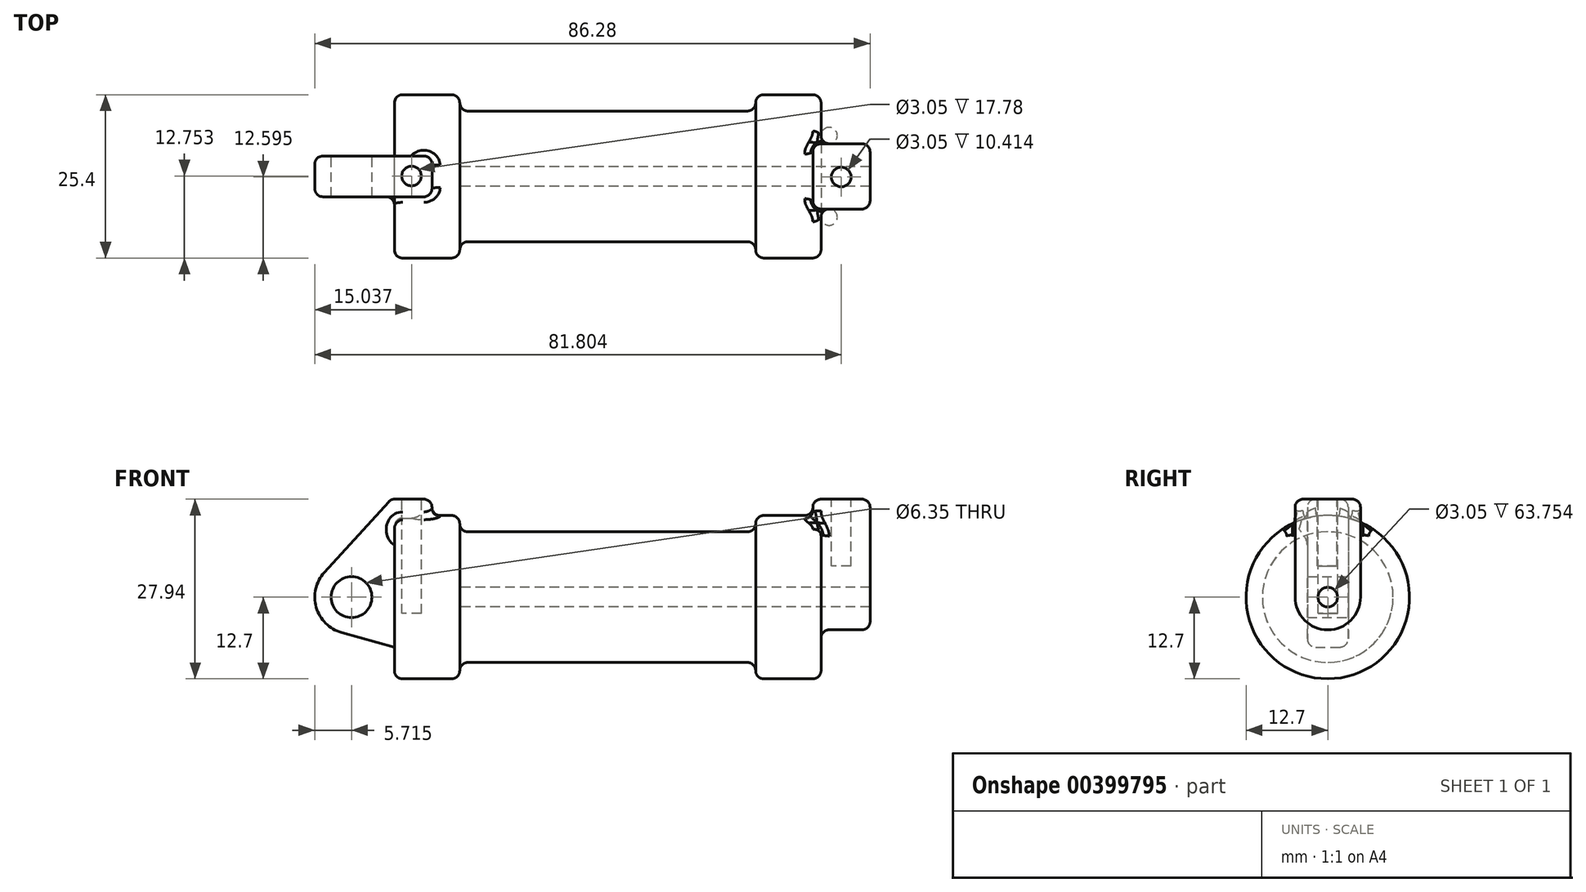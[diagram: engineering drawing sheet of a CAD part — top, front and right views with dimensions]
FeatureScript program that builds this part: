
annotation { "Feature Type Name" : "Feature", "Feature Type Description" : "" }
export const myFeature = defineFeature(function(context is Context, id is Id, definition is map)
    precondition{}
    {
        {
            var Q0;
            Q0=qCreatedBy(makeId("Front.planeOp"),FACE);
            var sketch = newSketch(context, id + "F0", { "sketchPlane" : qUnion([Q0])});
            skLineSegment(sketch, "E0", {"start": v(0, 0) * mm, "end": v(0, 12.7) * mm});
            skLineSegment(sketch, "E1", {"start": v(0, 12.7) * mm, "end": v(10.16, 12.7) * mm});
            skLineSegment(sketch, "E2", {"start": v(10.16, 12.7) * mm, "end": v(10.16, 10.16) * mm});
            skLineSegment(sketch, "E3", {"start": v(10.16, 10.16) * mm, "end": v(56.13, 10.16) * mm});
            skLineSegment(sketch, "E4", {"start": v(56.13, 10.16) * mm, "end": v(56.13, 12.7) * mm});
            skLineSegment(sketch, "E5", {"start": v(56.13, 12.7) * mm, "end": v(66.3, 12.7) * mm});
            skLineSegment(sketch, "E6", {"start": v(66.3, 12.7) * mm, "end": v(66.3, 0) * mm});
            skLineSegment(sketch, "E7", {"start": v(66.3, 0) * mm, "end": v(0, 0) * mm});
            skLineSegment(sketch, "E8", {"start": v(5.84, 15.24) * mm, "end": v(-0.5, 15.24) * mm});
            skLineSegment(sketch, "E9", {"start": v(-0.5, 15.24) * mm, "end": v(-10.88, 3.85) * mm});
            skLineSegment(sketch, "E10", {"start": v(0, 0) * mm, "end": v(-6.65, 0) * mm});
            skCircle(sketch, "E11", {"center": v(-6.65, 0) * mm, "radius": 5.72 * mm});
            skCircle(sketch, "E12", {"center": v(-6.65, 0) * mm, "radius": 3.18 * mm});
            skLineSegment(sketch, "E13", {"start": v(5.84, 15.24) * mm, "end": v(5.84, -9.4) * mm});
            skLineSegment(sketch, "E14", {"start": v(5.84, -9.4) * mm, "end": v(-8.18, -5.5) * mm});
            skSolve(sketch);
        }
        {
            var Q0;
            {var subQ0=sQuery(id+"F0.wireOp",EDGE,"E2");Q0=makeQuery(id+"F0.imprint","IMPRINT",FACE,{"disambiguationData":[TD([[makeQuery(id+"F0.imprint","IMPRINT",EDGE,{"derivedFrom":subQ0}),-1.0]])]});}
            var Q1;
            {var subQ0=sQuery(id+"F0.wireOp",EDGE,"E0");Q1=makeQuery(id+"F0.imprint","IMPRINT",FACE,{"disambiguationData":[TD([[makeQuery(id+"F0.imprint","IMPRINT",EDGE,{"derivedFrom":subQ0}),-1.0]])]});}
            var Q2;
            Q2=sQuery(id+"F0.wireOp",EDGE,"E7");
            revolve(context, id + "F1", {"entities" : qUnion([Q0, Q1]), "axis" : qUnion([Q2]), "revolveType" : RevolveType.FULL});
        }
        {
            var Q0;
            {var subQ1=sQuery(id+"F0.wireOp",EDGE,"E0");Q0=makeQuery(id+"F0.imprint","IMPRINT",FACE,{"disambiguationData":[TD([[makeQuery(id+"F0.imprint","IMPRINT",EDGE,{"derivedFrom":subQ1}),1.0]])]});}
            var Q1;
            {var subQ5=sQuery(id+"F0.wireOp",EDGE,"E12");Q1=makeQuery(id+"F0.imprint","IMPRINT",FACE,{"disambiguationData":[TD([[makeQuery(id+"F0.imprint","IMPRINT",EDGE,{"derivedFrom":subQ5}),-1.0]])]});}
            var Q2;
            {var subQ0=sQuery(id+"F0.wireOp",EDGE,"E14");Q2=makeQuery(id+"F0.imprint","IMPRINT",FACE,{"disambiguationData":[TD([[makeQuery(id+"F0.imprint","IMPRINT",EDGE,{"derivedFrom":subQ0}),-1.0]])]});}
            var Q3;
            {var subQ0=sQuery(id+"F0.wireOp",EDGE,"E0");Q3=makeQuery(id+"F0.imprint","IMPRINT",FACE,{"disambiguationData":[TD([[makeQuery(id+"F0.imprint","IMPRINT",EDGE,{"derivedFrom":subQ0}),-1.0]])]});}
            extrude(context, id + "F2", {"entities" : qUnion([Q0, Q1, Q2, Q3]), "operationType" : NewBodyOperationType.ADD, "depth" : 3.17 * mm, "hasSecondDirection" : true, "secondDirectionOppositeDirection" : true, "secondDirectionDepth" : 3.17 * mm});
        }
        {
            var Q0;
            Q0=makeQuery(id+"F1.opRevolve","SWEPT_FACE",FACE,{"disambiguationData":[OSD([sQuery(id+"F0.wireOp",EDGE,"E6")])]});
            var sketch = newSketch(context, id + "F3", { "sketchPlane" : qUnion([Q0])});
            skCircle(sketch, "E15", {"center": v(0, 0) * mm, "radius": 5.08 * mm});
            skCircle(sketch, "E16", {"center": v(0, 0) * mm, "radius": 1.52 * mm});
            skLineSegment(sketch, "E17", {"start": v(-5.08, 0) * mm, "end": v(-5.08, 15.24) * mm});
            skLineSegment(sketch, "E18", {"start": v(5.08, 0) * mm, "end": v(5.08, 15.24) * mm});
            skLineSegment(sketch, "E19", {"start": v(-5.08, 15.24) * mm, "end": v(5.08, 15.24) * mm});
            skSolve(sketch);
        }
        {
            var Q0;
            Q0=makeQuery(id+"F3.imprint","IMPRINT",FACE,{"disambiguationData":[TD([[makeQuery(id+"F3.imprint","IMPRINT",EDGE,{"derivedFrom":sQuery(id+"F3.wireOp",EDGE,"E16")}),-1.0]])]});
            var Q1;
            {var subQ0=sQuery(id+"F3.wireOp",EDGE,"E17");var subQ1=sQuery(id+"F3.wireOp",EDGE,"E15");var subQ2=makeQuery(id+"F3.imprint","INTERSECT",VERTEX,{"derivedFrom":[subQ1,subQ0]});Q1=makeQuery(id+"F3.imprint","IMPRINT",FACE,{"disambiguationData":[TD([[makeQuery(id+"F3.imprint","IMPRINT",EDGE,{"disambiguationData":[TD([[subQ2,1.0]])],"derivedFrom":subQ1}),-1.0]])]});}
            var Q2;
            {var subQ0=sQuery(id+"F3.wireOp",EDGE,"E19");Q2=makeQuery(id+"F3.imprint","IMPRINT",FACE,{"disambiguationData":[TD([[makeQuery(id+"F3.imprint","IMPRINT",EDGE,{"derivedFrom":subQ0}),-1.0]])]});}
            extrude(context, id + "F4", {"entities" : qUnion([Q0, Q1, Q2]), "operationType" : NewBodyOperationType.ADD, "depth" : 7.62 * mm, "hasSecondDirection" : true, "secondDirectionOppositeDirection" : true, "secondDirectionDepth" : 1.27 * mm});
        }
        {
            var Q0;
            Q0=makeQuery(id+"F2.opExtrude","SWEPT_FACE",FACE,{"disambiguationData":[OSD([sQuery(id+"F0.wireOp",EDGE,"E8")])]});
            var sketch = newSketch(context, id + "F5", { "sketchPlane" : qUnion([Q0])});
            skCircle(sketch, "E20", {"center": v(2.67, 0.05) * mm, "radius": 1.52 * mm});
            skPoint(sketch, "E20.centerSnap0", {"position": v(2.67, 3.18) * mm});
            skCircle(sketch, "E21", {"center": v(69.43, -0.1) * mm, "radius": 1.52 * mm});
            skSolve(sketch);
        }
        {
            var Q0;
            Q0=makeQuery(id+"F5.imprint","IMPRINT",FACE,{"disambiguationData":[TD([[makeQuery(id+"F5.imprint","IMPRINT",EDGE,{"derivedFrom":sQuery(id+"F5.wireOp",EDGE,"E20")}),1.0]])]});
            extrude(context, id + "F6", {"entities" : qUnion([Q0]), "operationType" : NewBodyOperationType.REMOVE, "oppositeDirection" : true, "depth" : 17.78 * mm});
        }
        {
            var Q0;
            Q0=makeQuery(id+"F4.boolean.opBoolean","SPLIT",FACE,{"disambiguationData":[TD([makeQuery(id+"F4.opExtrude","SWEPT_FACE",FACE,{"disambiguationData":[OSD([sQuery(id+"F3.wireOp",EDGE,"E16")])]})])],"derivedFrom":makeQuery(id+"F1.opRevolve","SWEPT_FACE",FACE,{"disambiguationData":[OSD([sQuery(id+"F0.wireOp",EDGE,"E6")])]})});
            var Q1;
            Q1=makeQuery(id+"F1.opRevolve","SWEPT_FACE",FACE,{"disambiguationData":[OSD([sQuery(id+"F0.wireOp",EDGE,"E2")])]});
            extrude(context, id + "F7", {"entities" : qUnion([Q0]), "operationType" : NewBodyOperationType.REMOVE, "endBound" : BoundingType.UP_TO_SURFACE, "oppositeDirection" : true, "endBoundEntityFace" : qUnion([Q1]), "depth" : 39.83 * mm});
        }
        {
            var Q0;
            Q0=makeQuery(id+"F5.imprint","IMPRINT",FACE,{"disambiguationData":[TD([[makeQuery(id+"F5.imprint","IMPRINT",EDGE,{"derivedFrom":sQuery(id+"F5.wireOp",EDGE,"E21")}),1.0]])]});
            extrude(context, id + "F8", {"entities" : qUnion([Q0]), "operationType" : NewBodyOperationType.REMOVE, "oppositeDirection" : true, "depth" : 10.4 * mm});
        }
        {
            var Q0;
            Q0=makeQuery(id+"F1.opRevolve","SWEPT_EDGE",EDGE,{"disambiguationData":[OSD([sQuery(id+"F0.wireOp",EDGE,"E1"),sQuery(id+"F0.wireOp",EDGE,"E2")])]});
            var Q1;
            Q1=makeQuery(id+"F1.opRevolve","SWEPT_EDGE",EDGE,{"disambiguationData":[OSD([sQuery(id+"F0.wireOp",EDGE,"E2"),sQuery(id+"F0.wireOp",EDGE,"E3")])]});
            var Q2;
            Q2=makeQuery(id+"F1.opRevolve","SWEPT_EDGE",EDGE,{"disambiguationData":[OSD([sQuery(id+"F0.wireOp",EDGE,"E4"),sQuery(id+"F0.wireOp",EDGE,"E5")])]});
            var Q3;
            Q3=makeQuery(id+"F1.opRevolve","SWEPT_FACE",FACE,{"disambiguationData":[OSD([sQuery(id+"F0.wireOp",EDGE,"E3")])]});
            var Q4;
            Q4=makeQuery(id+"F1.opRevolve","SWEPT_EDGE",EDGE,{"disambiguationData":[OSD([sQuery(id+"F0.wireOp",EDGE,"E0"),sQuery(id+"F0.wireOp",EDGE,"E1")])]});
            var Q5;
            Q5=makeQuery(id+"F1.opRevolve","SWEPT_EDGE",EDGE,{"disambiguationData":[OSD([sQuery(id+"F0.wireOp",EDGE,"E5"),sQuery(id+"F0.wireOp",EDGE,"E6")])]});
            var Q6;
            Q6=makeQuery(id+"F4.boolean.opBoolean","SPLIT",FACE,{"disambiguationData":[TD([makeQuery(id+"F1.opRevolve","SWEPT_FACE",FACE,{"disambiguationData":[OSD([sQuery(id+"F0.wireOp",EDGE,"E5")])]})])],"derivedFrom":makeQuery(id+"F1.opRevolve","SWEPT_FACE",FACE,{"disambiguationData":[OSD([sQuery(id+"F0.wireOp",EDGE,"E6")])]})});
            var Q7;
            Q7=makeQuery(id+"F4.opExtrude","SWEPT_EDGE",EDGE,{"disambiguationData":[OSD([sQuery(id+"F3.wireOp",EDGE,"E17"),sQuery(id+"F3.wireOp",EDGE,"E19")])]});
            var Q8;
            Q8=makeQuery(id+"F4.opExtrude","CAP_EDGE",EDGE,{"disambiguationData":[OSD([sQuery(id+"F3.wireOp",EDGE,"E19")])],"isStart":false});
            var Q9;
            Q9=makeQuery(id+"F4.opExtrude","SWEPT_EDGE",EDGE,{"disambiguationData":[OSD([sQuery(id+"F3.wireOp",EDGE,"E18"),sQuery(id+"F3.wireOp",EDGE,"E19")])]});
            var Q10;
            Q10=makeQuery(id+"F4.opExtrude","CAP_EDGE",EDGE,{"disambiguationData":[OSD([sQuery(id+"F3.wireOp",EDGE,"E19")])],"isStart":true});
            var Q11;
            Q11=makeQuery(id+"F2.opExtrude","CAP_EDGE",EDGE,{"disambiguationData":[OSD([sQuery(id+"F0.wireOp",EDGE,"E8")])],"isStart":true});
            var Q12;
            Q12=makeQuery(id+"F2.opExtrude","SWEPT_EDGE",EDGE,{"disambiguationData":[OSD([sQuery(id+"F0.wireOp",EDGE,"E8"),sQuery(id+"F0.wireOp",EDGE,"E9")])]});
            var Q13;
            Q13=makeQuery(id+"F2.opExtrude","CAP_EDGE",EDGE,{"disambiguationData":[OSD([sQuery(id+"F0.wireOp",EDGE,"E9")])],"isStart":true});
            var Q14;
            Q14=makeQuery(id+"F2.opExtrude","SWEPT_EDGE",EDGE,{"disambiguationData":[OSD([sQuery(id+"F0.wireOp",EDGE,"E8"),sQuery(id+"F0.wireOp",EDGE,"E13")])]});
            var Q15;
            Q15=makeQuery(id+"F2.boolean.opBoolean","INTERSECT",EDGE,{"derivedFrom":[makeQuery(id+"F1.opRevolve","SWEPT_FACE",FACE,{"disambiguationData":[OSD([sQuery(id+"F0.wireOp",EDGE,"E1")])]}),makeQuery(id+"F2.opExtrude","SWEPT_FACE",FACE,{"disambiguationData":[OSD([sQuery(id+"F0.wireOp",EDGE,"E13")])]})]});
            var Q16;
            Q16=makeQuery(id+"F4.opExtrude","CAP_EDGE",EDGE,{"disambiguationData":[OSD([sQuery(id+"F3.wireOp",EDGE,"E17")])],"isStart":true});
            var Q17;
            Q17=makeQuery(id+"F4.boolean.opBoolean","INTERSECT",EDGE,{"derivedFrom":[makeQuery(id+"F1.opRevolve","SWEPT_FACE",FACE,{"disambiguationData":[OSD([sQuery(id+"F0.wireOp",EDGE,"E5")])]}),makeQuery(id+"F4.opExtrude","CAP_FACE",FACE,{"disambiguationData":[OSD([sQuery(id+"F3.wireOp",EDGE,"E15"),sQuery(id+"F3.wireOp",EDGE,"E16"),sQuery(id+"F3.wireOp",EDGE,"E17"),sQuery(id+"F3.wireOp",EDGE,"E18"),sQuery(id+"F3.wireOp",EDGE,"E19")])],"isStart":true})]});
            var Q18;
            Q18=makeQuery(id+"F4.opExtrude","CAP_EDGE",EDGE,{"disambiguationData":[OSD([sQuery(id+"F3.wireOp",EDGE,"E18")])],"isStart":true});
            var Q19;
            Q19=makeQuery(id+"F4.boolean.opBoolean","INTERSECT",EDGE,{"derivedFrom":[makeQuery(id+"F1.opRevolve","SWEPT_FACE",FACE,{"disambiguationData":[OSD([sQuery(id+"F0.wireOp",EDGE,"E5")])]}),makeQuery(id+"F4.opExtrude","SWEPT_FACE",FACE,{"disambiguationData":[OSD([sQuery(id+"F3.wireOp",EDGE,"E17")])]})]});
            var Q20;
            Q20=makeQuery(id+"F4.boolean.opBoolean","INTERSECT",EDGE,{"derivedFrom":[makeQuery(id+"F1.opRevolve","SWEPT_FACE",FACE,{"disambiguationData":[OSD([sQuery(id+"F0.wireOp",EDGE,"E5")])]}),makeQuery(id+"F4.opExtrude","SWEPT_FACE",FACE,{"disambiguationData":[OSD([sQuery(id+"F3.wireOp",EDGE,"E18")])]})]});
            var Q21;
            Q21=makeQuery(id+"F4.opExtrude","CAP_EDGE",EDGE,{"disambiguationData":[OSD([sQuery(id+"F3.wireOp",EDGE,"E18")])],"isStart":false});
            var Q22;
            Q22=makeQuery(id+"F4.opExtrude","CAP_EDGE",EDGE,{"disambiguationData":[OSD([sQuery(id+"F3.wireOp",EDGE,"E17")])],"isStart":false});
            var Q23;
            Q23=makeQuery(id+"F4.opExtrude","CAP_EDGE",EDGE,{"disambiguationData":[OSD([sQuery(id+"F3.wireOp",EDGE,"E15")])],"isStart":false});
            var Q24;
            Q24=makeQuery(id+"F2.opExtrude","CAP_EDGE",EDGE,{"disambiguationData":[OSD([sQuery(id+"F0.wireOp",EDGE,"E11")])],"isStart":false});
            var Q25;
            Q25=makeQuery(id+"F2.opExtrude","CAP_EDGE",EDGE,{"disambiguationData":[OSD([sQuery(id+"F0.wireOp",EDGE,"E8")])],"isStart":false});
            var Q26;
            Q26=makeQuery(id+"F2.opExtrude","CAP_EDGE",EDGE,{"disambiguationData":[OSD([sQuery(id+"F0.wireOp",EDGE,"E13")])],"isStart":false});
            var Q27;
            Q27=makeQuery(id+"F2.boolean.opBoolean","INTERSECT",EDGE,{"derivedFrom":[makeQuery(id+"F1.opRevolve","SWEPT_FACE",FACE,{"disambiguationData":[OSD([sQuery(id+"F0.wireOp",EDGE,"E1")])]}),makeQuery(id+"F2.opExtrude","CAP_FACE",FACE,{"disambiguationData":[OSD([sQuery(id+"F0.wireOp",EDGE,"E8"),sQuery(id+"F0.wireOp",EDGE,"E9"),sQuery(id+"F0.wireOp",EDGE,"E11"),sQuery(id+"F0.wireOp",EDGE,"E12"),sQuery(id+"F0.wireOp",EDGE,"E13"),sQuery(id+"F0.wireOp",EDGE,"E14")])],"isStart":false})]});
            var Q28;
            Q28=makeQuery(id+"F2.opExtrude","CAP_EDGE",EDGE,{"disambiguationData":[OSD([sQuery(id+"F0.wireOp",EDGE,"E13")])],"isStart":true});
            fillet(context, id + "F9", {"entities" : qUnion([Q0, Q1, Q2, Q3, Q4, Q5, Q6, Q7, Q8, Q9, Q10, Q11, Q12, Q13, Q14, Q15, Q16, Q17, Q18, Q19, Q20, Q21, Q22, Q23, Q24, Q25, Q26, Q27, Q28]), "radius" : 1.27 * mm, "tangentPropagation" : true, "allowEdgeOverflow" : false});
        }
    });
